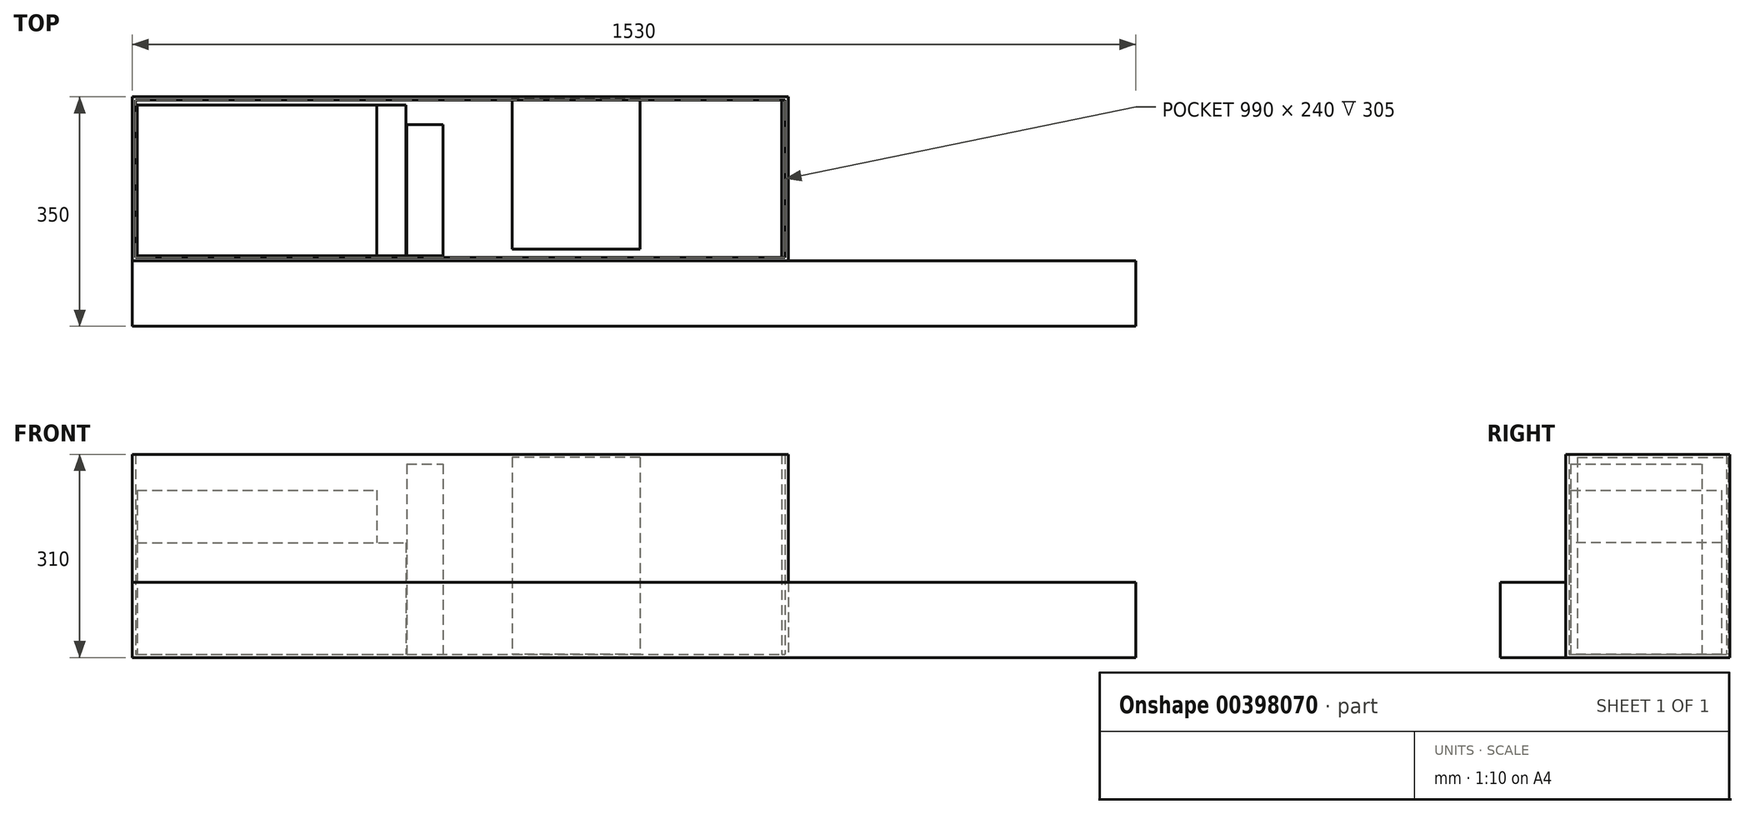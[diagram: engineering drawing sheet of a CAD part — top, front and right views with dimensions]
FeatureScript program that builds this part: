
annotation { "Feature Type Name" : "Feature", "Feature Type Description" : "" }
export const myFeature = defineFeature(function(context is Context, id is Id, definition is map)
    precondition{}
    {
        {
            var Q0;
            Q0=qCreatedBy(makeId("Top.planeOp"),FACE);
            var sketch = newSketch(context, id + "F0", { "sketchPlane" : qUnion([Q0])});
            skLineSegment(sketch, "E0.bottom", {"start": v(0, 0) * mm, "end": v(1000, 0) * mm});
            skLineSegment(sketch, "E0.top", {"start": v(0, 250) * mm, "end": v(1000, 250) * mm});
            skLineSegment(sketch, "E0.left", {"start": v(0, 0) * mm, "end": v(0, 250) * mm});
            skLineSegment(sketch, "E0.right", {"start": v(1000, 0) * mm, "end": v(1000, 250) * mm});
            skSolve(sketch);
        }
        {
            var Q0;
            Q0=qSketchRegion(id+"F0",true);
            extrude(context, id + "F1", {"entities" : qUnion([Q0]), "depth" : 310 * mm});
        }
        {
            var Q0;
            Q0=makeQuery(id+"F1.opExtrude","CAP_FACE",FACE,{"disambiguationData":[OSD([sQuery(id+"F0.wireOp",EDGE,"E0.bottom"),sQuery(id+"F0.wireOp",EDGE,"E0.top"),sQuery(id+"F0.wireOp",EDGE,"E0.left"),sQuery(id+"F0.wireOp",EDGE,"E0.right")])],"isStart":false});
            shell(context, id + "F2", {"entities" : qUnion([Q0]), "thickness" : 5 * mm});
        }
        {
            var Q0;
            Q0=makeQuery(id+"F2.opShell","OFFSET_FACE",FACE,{"disambiguationData":[OSD([sQuery(id+"F0.wireOp",EDGE,"E0.bottom"),sQuery(id+"F0.wireOp",EDGE,"E0.top"),sQuery(id+"F0.wireOp",EDGE,"E0.left"),sQuery(id+"F0.wireOp",EDGE,"E0.right")])]});
            var sketch = newSketch(context, id + "F3", { "sketchPlane" : qUnion([Q0])});
            skLineSegment(sketch, "E1.bottom", {"start": v(7.5, 237.5) * mm, "end": v(417.5, 237.5) * mm});
            skLineSegment(sketch, "E1.top", {"start": v(7.5, 7.5) * mm, "end": v(417.5, 7.5) * mm});
            skLineSegment(sketch, "E1.left", {"start": v(7.5, 237.5) * mm, "end": v(7.5, 7.5) * mm});
            skLineSegment(sketch, "E1.right", {"start": v(417.5, 237.5) * mm, "end": v(417.5, 7.5) * mm});
            skSolve(sketch);
        }
        {
            var Q0;
            Q0=qSketchRegion(id+"F3",true);
            extrude(context, id + "F4", {"entities" : qUnion([Q0]), "depth" : 170 * mm});
        }
        {
            var Q0;
            Q0=makeQuery(id+"F4.opExtrude","CAP_FACE",FACE,{"disambiguationData":[OSD([sQuery(id+"F3.wireOp",EDGE,"E1.bottom"),sQuery(id+"F3.wireOp",EDGE,"E1.top"),sQuery(id+"F3.wireOp",EDGE,"E1.left"),sQuery(id+"F3.wireOp",EDGE,"E1.right")])],"isStart":false});
            var sketch = newSketch(context, id + "F5", { "sketchPlane" : qUnion([Q0])});
            skLineSegment(sketch, "E2.bottom", {"start": v(7.5, 7.5) * mm, "end": v(372.5, 7.5) * mm});
            skLineSegment(sketch, "E2.top", {"start": v(7.5, 237.5) * mm, "end": v(372.5, 237.5) * mm});
            skLineSegment(sketch, "E2.left", {"start": v(7.5, 7.5) * mm, "end": v(7.5, 237.5) * mm});
            skLineSegment(sketch, "E2.right", {"start": v(372.5, 7.5) * mm, "end": v(372.5, 237.5) * mm});
            skSolve(sketch);
        }
        {
            var Q0;
            Q0=qSketchRegion(id+"F5",true);
            extrude(context, id + "F6", {"entities" : qUnion([Q0]), "depth" : 80 * mm});
        }
        {
            var Q0;
            Q0=makeQuery(id+"F2.opShell","OFFSET_FACE",FACE,{"disambiguationData":[OSD([sQuery(id+"F0.wireOp",EDGE,"E0.bottom"),sQuery(id+"F0.wireOp",EDGE,"E0.top"),sQuery(id+"F0.wireOp",EDGE,"E0.left"),sQuery(id+"F0.wireOp",EDGE,"E0.right")])]});
            var sketch = newSketch(context, id + "F7", { "sketchPlane" : qUnion([Q0])});
            skLineSegment(sketch, "E3.bottom", {"start": v(418.5, 7.5) * mm, "end": v(473.5, 7.5) * mm});
            skLineSegment(sketch, "E3.top", {"start": v(418.5, 207.5) * mm, "end": v(473.5, 207.5) * mm});
            skLineSegment(sketch, "E3.left", {"start": v(418.5, 7.5) * mm, "end": v(418.5, 207.5) * mm});
            skLineSegment(sketch, "E3.right", {"start": v(473.5, 7.5) * mm, "end": v(473.5, 207.5) * mm});
            skSolve(sketch);
        }
        {
            var Q0;
            Q0=qSketchRegion(id+"F7",true);
            extrude(context, id + "F8", {"entities" : qUnion([Q0]), "depth" : 290 * mm});
        }
        {
            var Q0;
            Q0=makeQuery(id+"F2.opShell","OFFSET_FACE",FACE,{"disambiguationData":[OSD([sQuery(id+"F0.wireOp",EDGE,"E0.bottom"),sQuery(id+"F0.wireOp",EDGE,"E0.top"),sQuery(id+"F0.wireOp",EDGE,"E0.left"),sQuery(id+"F0.wireOp",EDGE,"E0.right")])]});
            var sketch = newSketch(context, id + "F9", { "sketchPlane" : qUnion([Q0])});
            skLineSegment(sketch, "E4.bottom", {"start": v(774.11, 17.7) * mm, "end": v(579.11, 17.7) * mm});
            skLineSegment(sketch, "E4.top", {"start": v(774.11, 247.7) * mm, "end": v(579.11, 247.7) * mm});
            skLineSegment(sketch, "E4.left", {"start": v(774.11, 17.7) * mm, "end": v(774.11, 247.7) * mm});
            skLineSegment(sketch, "E4.right", {"start": v(579.11, 17.7) * mm, "end": v(579.11, 247.7) * mm});
            skSolve(sketch);
        }
        {
            var Q0;
            Q0=qSketchRegion(id+"F9",true);
            extrude(context, id + "F10", {"entities" : qUnion([Q0]), "depth" : 300 * mm});
        }
        {
            var Q0;
            Q0=qCreatedBy(makeId("Top.planeOp"),FACE);
            var sketch = newSketch(context, id + "F11", { "sketchPlane" : qUnion([Q0])});
            skLineSegment(sketch, "E5.bottom", {"start": v(0, 0) * mm, "end": v(1530, 0) * mm});
            skLineSegment(sketch, "E5.top", {"start": v(0, -100) * mm, "end": v(1530, -100) * mm});
            skLineSegment(sketch, "E5.left", {"start": v(0, 0) * mm, "end": v(0, -100) * mm});
            skLineSegment(sketch, "E5.right", {"start": v(1530, 0) * mm, "end": v(1530, -100) * mm});
            skSolve(sketch);
        }
        {
            var Q0;
            Q0=makeQuery(id+"F11.imprint","IMPRINT",FACE,{"disambiguationData":[TD([[makeQuery(id+"F11.imprint","IMPRINT",EDGE,{"derivedFrom":sQuery(id+"F11.wireOp",EDGE,"E5.bottom")}),-1.0]])]});
            extrude(context, id + "F12", {"entities" : qUnion([Q0]), "depth" : 115 * mm});
        }
        {
            var Q0;
            Q0=makeQuery(id+"F2.opShell","OFFSET_FACE",FACE,{"disambiguationData":[OSD([sQuery(id+"F0.wireOp",EDGE,"E0.right")])]});
            var sketch = newSketch(context, id + "F13", { "sketchPlane" : qUnion([Q0])});
            skLineSegment(sketch, "E6.bottom", {"start": v(-245, 310) * mm, "end": v(-5, 310) * mm});
            skLineSegment(sketch, "E6.top", {"start": v(-245, 5) * mm, "end": v(-5, 5) * mm});
            skLineSegment(sketch, "E6.left", {"start": v(-245, 310) * mm, "end": v(-245, 5) * mm});
            skLineSegment(sketch, "E6.right", {"start": v(-5, 310) * mm, "end": v(-5, 5) * mm});
            skSolve(sketch);
        }
        {
            var Q0;
            Q0=qSketchRegion(id+"F13",true);
            extrude(context, id + "F14", {"entities" : qUnion([Q0]), "depth" : 5 * mm});
        }
    });
